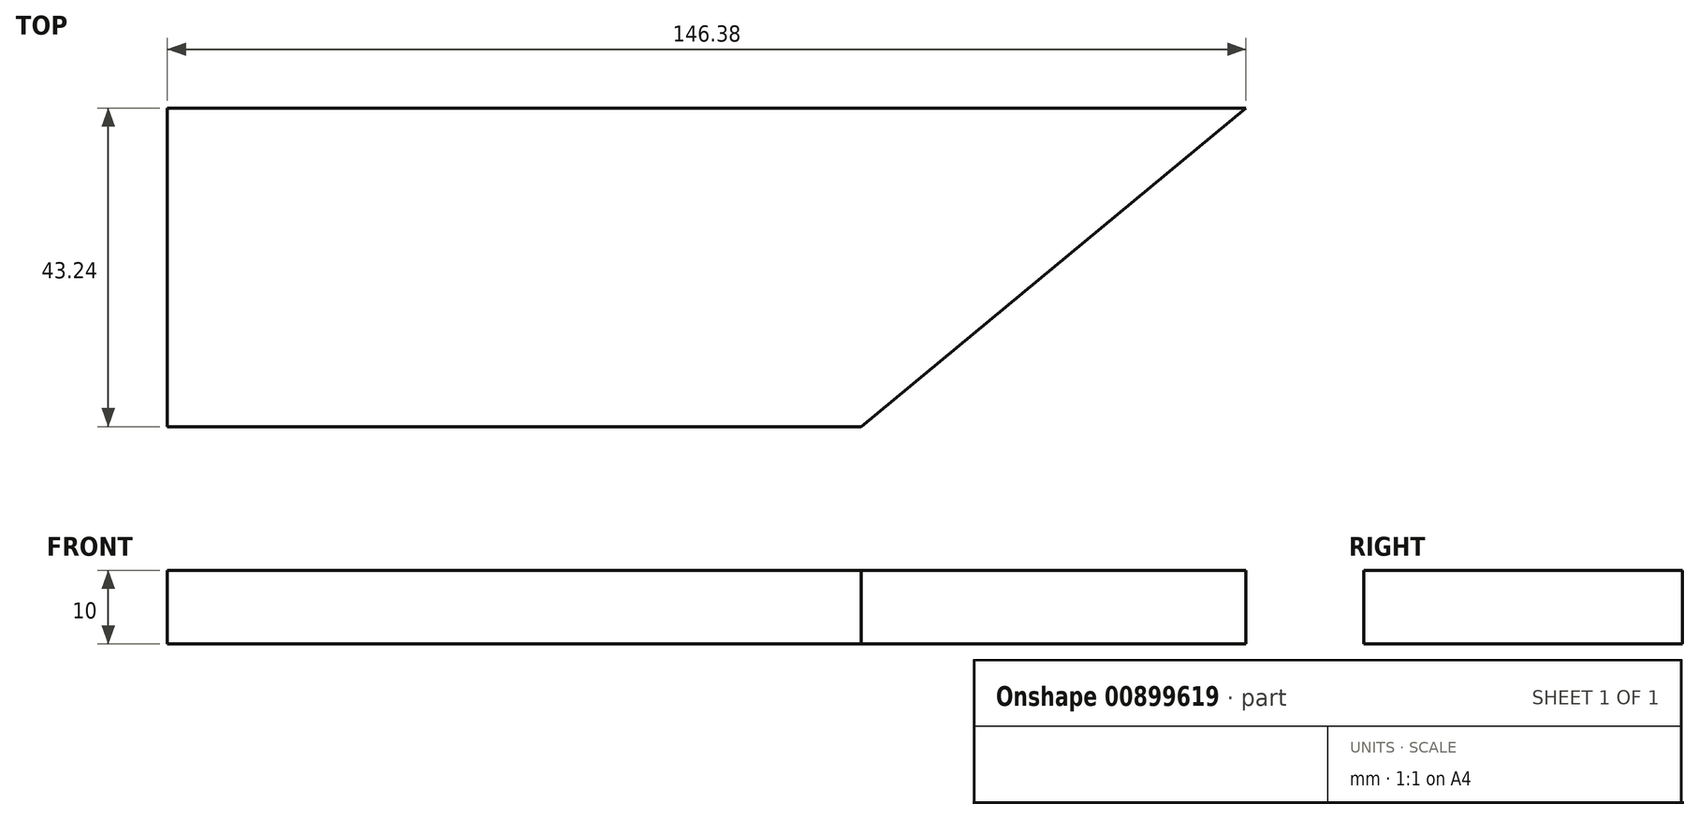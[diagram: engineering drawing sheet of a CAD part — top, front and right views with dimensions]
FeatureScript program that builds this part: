
annotation { "Feature Type Name" : "Feature", "Feature Type Description" : "" }
export const myFeature = defineFeature(function(context is Context, id is Id, definition is map)
    precondition{}
    {
        {
            var Q0;
            Q0=qCreatedBy(makeId("Top.planeOp"),FACE);
            var sketch = newSketch(context, id + "F0", { "sketchPlane" : qUnion([Q0])});
            skLineSegment(sketch, "E0.bottom", {"start": v(47.07, -21.62) * mm, "end": v(-47.07, -21.62) * mm});
            skLineSegment(sketch, "E0.top", {"start": v(47.07, 21.62) * mm, "end": v(-47.07, 21.62) * mm});
            skLineSegment(sketch, "E0.left", {"start": v(47.07, -21.62) * mm, "end": v(47.07, 21.62) * mm});
            skLineSegment(sketch, "E0.right", {"start": v(-47.07, -21.62) * mm, "end": v(-47.07, 21.62) * mm});
            skPoint(sketch, "E0.middle", {"position": v(0, 0) * mm});
            skLineSegment(sketch, "E1", {"start": v(47.07, 21.62) * mm, "end": v(99.3, 21.62) * mm});
            skLineSegment(sketch, "E2", {"start": v(99.3, 21.62) * mm, "end": v(47.07, -21.62) * mm});
            skSolve(sketch);
        }
        {
            var Q0;
            Q0=makeQuery(id+"F0.imprint","IMPRINT",FACE,{"disambiguationData":[TD([[makeQuery(id+"F0.imprint","IMPRINT",EDGE,{"derivedFrom":sQuery(id+"F0.wireOp",EDGE,"E0.left")}),-1.0]])]});
            var Q1;
            Q1=makeQuery(id+"F0.imprint","IMPRINT",FACE,{"disambiguationData":[TD([[makeQuery(id+"F0.imprint","IMPRINT",EDGE,{"derivedFrom":sQuery(id+"F0.wireOp",EDGE,"E0.bottom")}),-1.0]])]});
            extrude(context, id + "F1", {"entities" : qUnion([Q0, Q1]), "depth" : 10 * mm, "offsetDistance" : 25.4 * mm});
        }
    });
